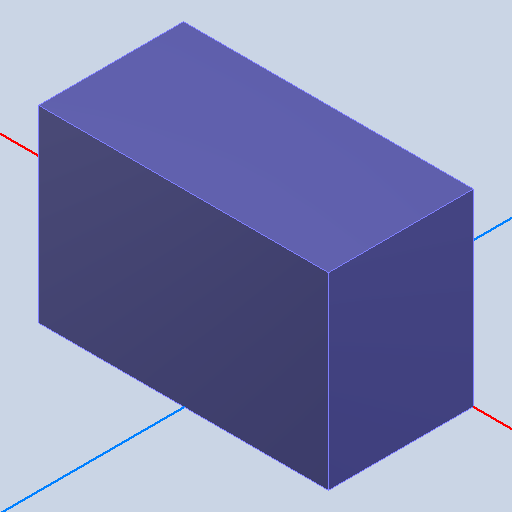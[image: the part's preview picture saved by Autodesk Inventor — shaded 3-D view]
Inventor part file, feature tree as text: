
AUTODESK INVENTOR PART (.ipt)
format: ipt  version: 2022 (Build 260153000, 153)  size: 94,208 bytes
history: native  units: mm
features: other x2, extrude x1
ambient origin geometry x8: Origin, YZ Plane, XZ Plane, XY Plane, X Axis, Y Axis, Z Axis, Center Point
bodies: Body1 (feature_tree)
feature tree (3):
  other  "Твердое тело1"
  extrude  "Выдавливание1"  Depth=1.0mm TaperAngle=0.0deg
  other  "C0805K, C0805K_1"
